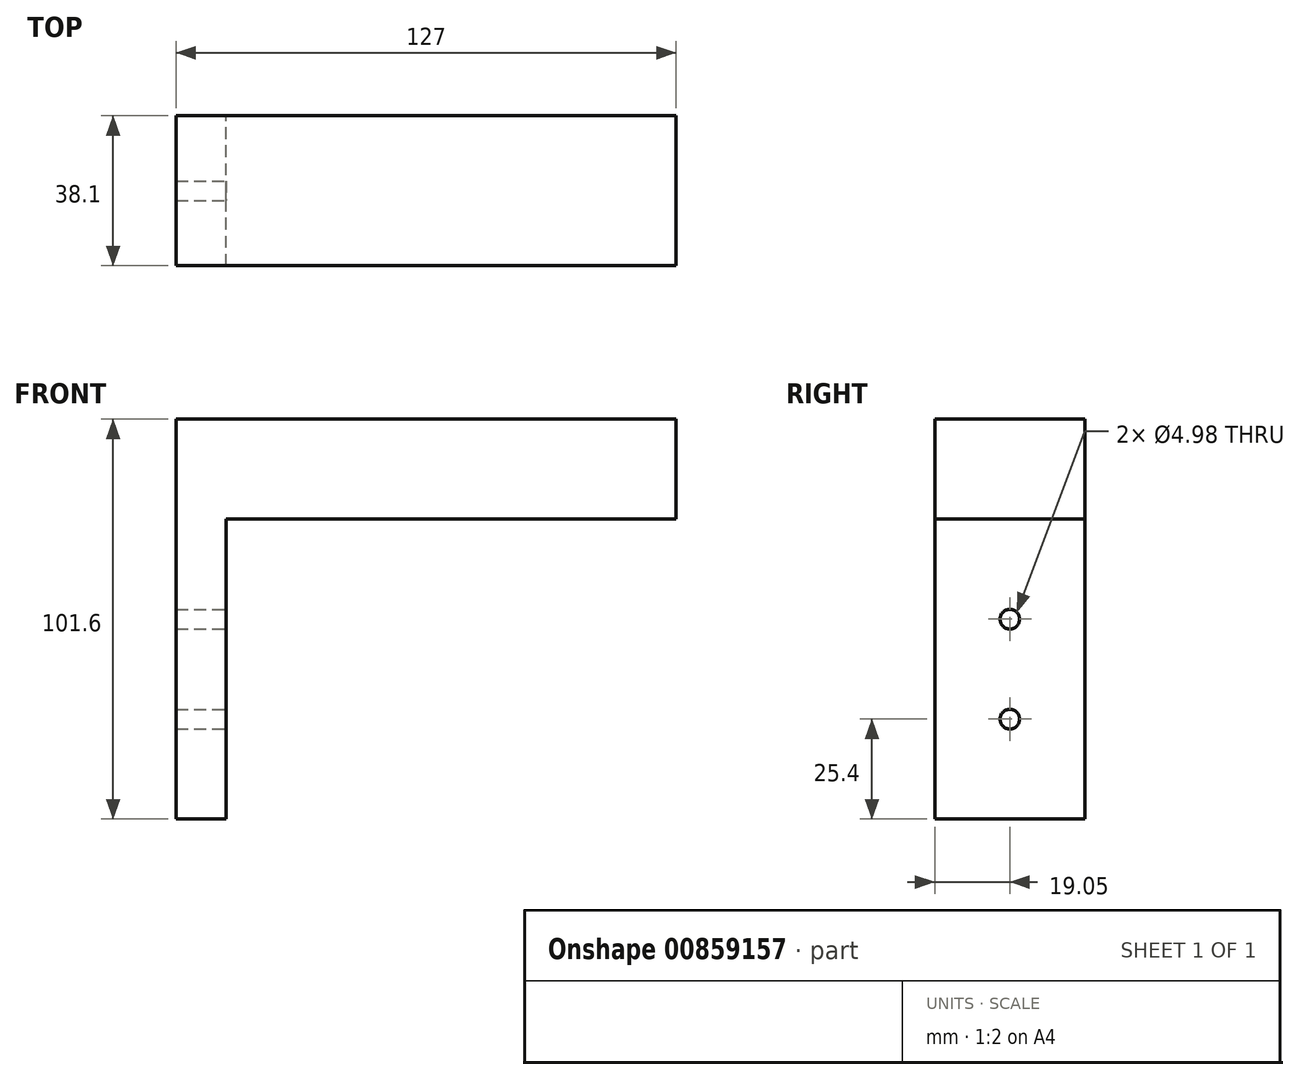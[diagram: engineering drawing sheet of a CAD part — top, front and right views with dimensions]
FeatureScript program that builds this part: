
annotation { "Feature Type Name" : "Feature", "Feature Type Description" : "" }
export const myFeature = defineFeature(function(context is Context, id is Id, definition is map)
    precondition{}
    {
        {
            var Q0;
            Q0=qCreatedBy(makeId("Front.planeOp"),FACE);
            var sketch = newSketch(context, id + "F0", { "sketchPlane" : qUnion([Q0])});
            skLineSegment(sketch, "E0", {"start": v(0, 0) * mm, "end": v(0, 101.6) * mm});
            skLineSegment(sketch, "E1", {"start": v(0, 101.6) * mm, "end": v(127, 101.6) * mm});
            skLineSegment(sketch, "E2", {"start": v(127, 101.6) * mm, "end": v(127, 76.2) * mm});
            skLineSegment(sketch, "E3", {"start": v(127, 76.2) * mm, "end": v(12.7, 76.2) * mm});
            skLineSegment(sketch, "E4", {"start": v(12.7, 76.2) * mm, "end": v(12.7, 0) * mm});
            skLineSegment(sketch, "E5", {"start": v(12.7, 0) * mm, "end": v(0, 0) * mm});
            skSolve(sketch);
        }
        {
            var Q0;
            Q0 = qSketchRegion(id + "F0", true);
            extrude(context, id + "F1", {"entities" : qUnion([Q0]), "depth" : 38.1 * mm, "offsetDistance" : 25.4 * mm});
        }
        {
            var Q0;
            Q0=makeQuery(id+"F1.opExtrude","SWEPT_FACE",FACE,{"disambiguationData":[OSD([sQuery(id+"F0.wireOp",EDGE,"E4")])]});
            var sketch = newSketch(context, id + "F2", { "sketchPlane" : qUnion([Q0])});
            skCircle(sketch, "E6", {"center": v(-19.05, 50.8) * mm, "radius": 2.49 * mm});
            skCircle(sketch, "E7", {"center": v(-19.05, 25.4) * mm, "radius": 2.49 * mm});
            skLineSegment(sketch, "E8", {"start": v(-19.05, 50.8) * mm, "end": v(0, 50.8) * mm, "construction": true});
            skLineSegment(sketch, "E9", {"start": v(-19.05, 50.8) * mm, "end": v(-38.1, 50.8) * mm, "construction": true});
            skLineSegment(sketch, "E10", {"start": v(-19.05, 50.8) * mm, "end": v(-19.05, 25.4) * mm, "construction": true});
            skLineSegment(sketch, "E11", {"start": v(-19.05, 25.4) * mm, "end": v(-19.05, 0) * mm, "construction": true});
            skLineSegment(sketch, "E12", {"start": v(-19.05, 76.2) * mm, "end": v(-19.05, 50.8) * mm, "construction": true});
            skSolve(sketch);
        }
        {
            var Q0;
            Q0 = qSketchRegion(id + "F2", true);
            extrude(context, id + "F3", {"entities" : qUnion([Q0]), "operationType" : NewBodyOperationType.REMOVE, "endBound" : BoundingType.THROUGH_ALL, "oppositeDirection" : true, "depth" : 25.4 * mm, "offsetDistance" : 25.4 * mm});
        }
    });
